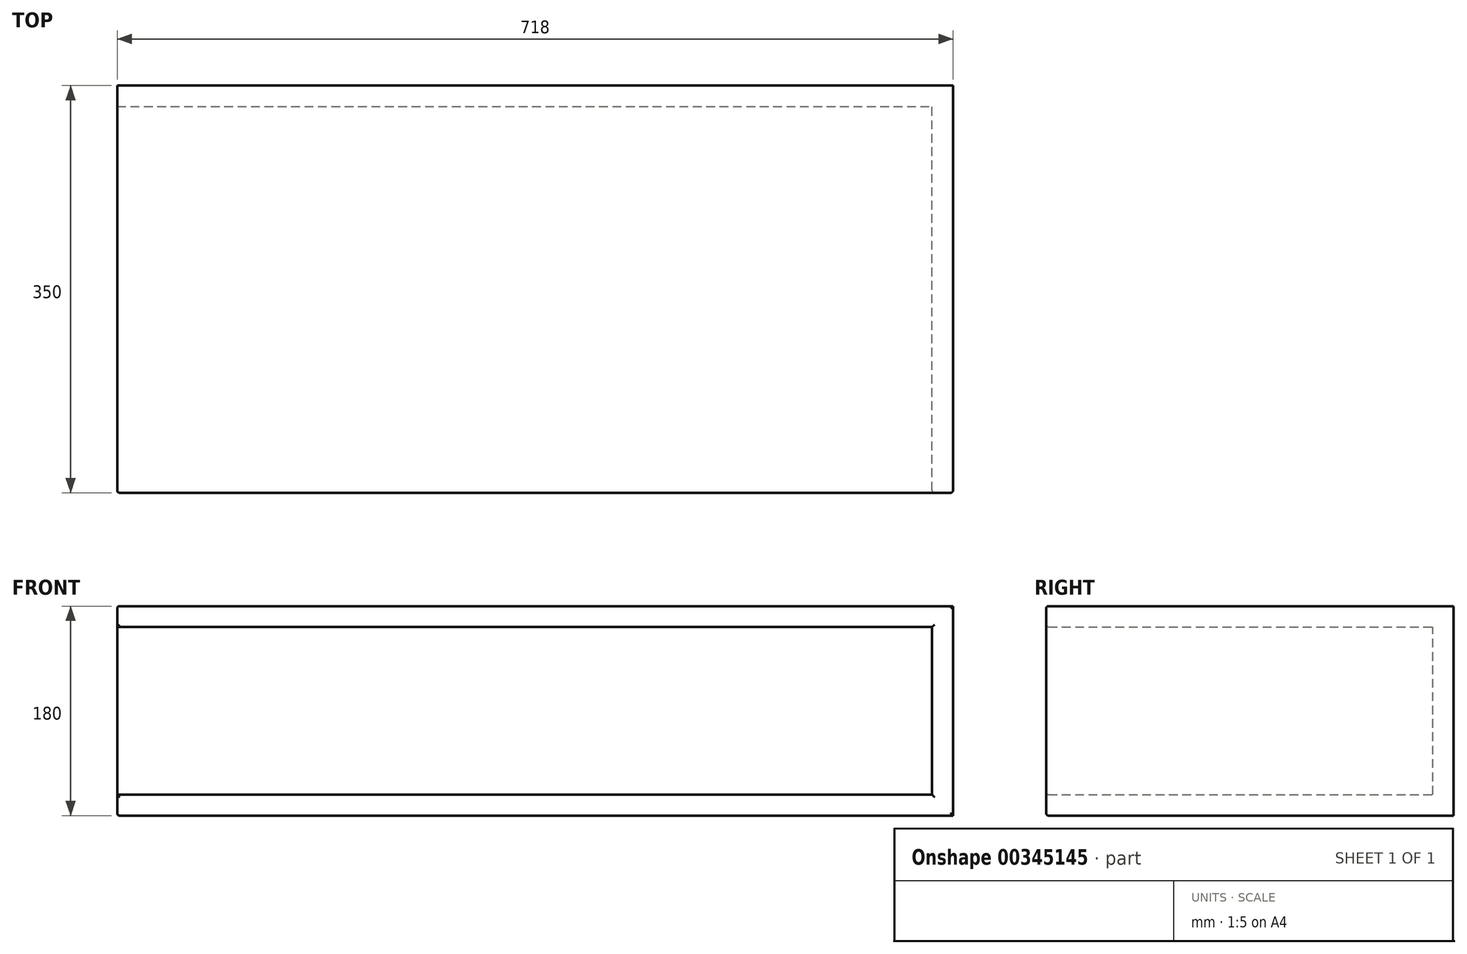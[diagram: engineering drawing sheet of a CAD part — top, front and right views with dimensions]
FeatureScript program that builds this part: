
annotation { "Feature Type Name" : "Feature", "Feature Type Description" : "" }
export const myFeature = defineFeature(function(context is Context, id is Id, definition is map)
    precondition{}
    {
        {
            var Q0;
            Q0=qCreatedBy(makeId("Front.planeOp"),FACE);
            var sketch = newSketch(context, id + "F0", { "sketchPlane" : qUnion([Q0])});
            skLineSegment(sketch, "E0.bottom", {"start": v(0, 0) * mm, "end": v(35.38, 0) * mm});
            skLineSegment(sketch, "E0.top", {"start": v(0, 39.43) * mm, "end": v(35.38, 39.43) * mm});
            skLineSegment(sketch, "E0.left", {"start": v(0, 0) * mm, "end": v(0, 39.43) * mm});
            skLineSegment(sketch, "E0.right", {"start": v(35.38, 0) * mm, "end": v(35.38, 39.43) * mm});
            skSolve(sketch);
        }
        {
            var Q0;
            Q0=makeQuery(id+"F0.imprint","IMPRINT",FACE,{"disambiguationData":[TD([[makeQuery(id+"F0.imprint","IMPRINT",EDGE,{"derivedFrom":sQuery(id+"F0.wireOp",EDGE,"E0.bottom")}),1.0]])]});
            extrude(context, id + "F1", {"entities" : qUnion([Q0]), "depth" : 350 * mm});
        }
        {
            var Q0;
            Q0=makeQuery(id+"F1.opExtrude","SWEPT_FACE",FACE,{"disambiguationData":[OSD([sQuery(id+"F0.wireOp",EDGE,"E0.left")])]});
            extrude(context, id + "F2", {"entities" : qUnion([Q0]), "operationType" : NewBodyOperationType.ADD, "oppositeDirection" : true, "depth" : 718 * mm});
        }
        {
            var Q0;
            {var subQ0=sQuery(id+"F0.wireOp",EDGE,"E0.bottom");Q0=makeQuery(id+"F2.boolean.opBoolean","MERGE",FACE,{"derivedFrom":[makeQuery(id+"F1.opExtrude","SWEPT_FACE",FACE,{"disambiguationData":[OSD([subQ0])]}),makeQuery(id+"F2.opExtrude","SWEPT_FACE",FACE,{"disambiguationData":[OSD([subQ0,sQuery(id+"F0.wireOp",EDGE,"E0.left")])]})]});}
            extrude(context, id + "F3", {"entities" : qUnion([Q0]), "operationType" : NewBodyOperationType.ADD, "oppositeDirection" : true, "depth" : 180 * mm});
        }
        {
            var Q0;
            {var subQ0=sQuery(id+"F0.wireOp",EDGE,"E0.left");var subQ1=sQuery(id+"F0.wireOp",EDGE,"E0.bottom");Q0=makeQuery(id+"F3.boolean.opBoolean","MERGE",FACE,{"derivedFrom":[makeQuery(id+"F2.boolean.opBoolean","MERGE",FACE,{"derivedFrom":[makeQuery(id+"F1.opExtrude","CAP_FACE",FACE,{"disambiguationData":[OSD([subQ1,sQuery(id+"F0.wireOp",EDGE,"E0.top"),subQ0,sQuery(id+"F0.wireOp",EDGE,"E0.right")])],"isStart":false}),makeQuery(id+"F2.opExtrude","SWEPT_FACE",FACE,{"disambiguationData":[OSD([subQ0]),TDD([makeQuery(id+"F1.opExtrude","CAP_EDGE",EDGE,{"disambiguationData":[OSD([subQ0])],"isStart":false})])]})]}),makeQuery(id+"F3.opExtrude","SWEPT_FACE",FACE,{"disambiguationData":[OSD([subQ1,subQ0]),TDD([makeQuery(id+"F2.boolean.opBoolean","MERGE",EDGE,{"derivedFrom":[makeQuery(id+"F1.opExtrude","CAP_EDGE",EDGE,{"disambiguationData":[OSD([subQ1])],"isStart":false}),makeQuery(id+"F2.opExtrude","SWEPT_EDGE",EDGE,{"disambiguationData":[OSD([subQ1,subQ0]),TDD([makeQuery(id+"F1.opExtrude","CAP_VERTEX",VERTEX,{"disambiguationData":[OSD([subQ1,subQ0])],"isStart":false})])]})]})])]})]});}
            var Q1;
            {var subQ0=sQuery(id+"F0.wireOp",EDGE,"E0.left");var subQ1=sQuery(id+"F0.wireOp",EDGE,"E0.bottom");Q1=makeQuery(id+"F3.boolean.opBoolean","MERGE",FACE,{"derivedFrom":[makeQuery(id+"F1.opExtrude","SWEPT_FACE",FACE,{"disambiguationData":[OSD([subQ0])]}),makeQuery(id+"F3.opExtrude","SWEPT_FACE",FACE,{"disambiguationData":[OSD([subQ1,subQ0]),TDD([makeQuery(id+"F1.opExtrude","SWEPT_EDGE",EDGE,{"disambiguationData":[OSD([subQ1,subQ0])]})])]})]});}
            shell(context, id + "F4", {"entities" : qUnion([Q0, Q1]), "thickness" : 18 * mm});
        }
        {
            var Q0;
            {var subQ0=sQuery(id+"F0.wireOp",EDGE,"E0.left");var subQ1=sQuery(id+"F0.wireOp",EDGE,"E0.bottom");Q0=makeQuery(id+"F3.opExtrude","CAP_EDGE",EDGE,{"disambiguationData":[OSD([subQ1,subQ0]),TDD([makeQuery(id+"F2.boolean.opBoolean","MERGE",EDGE,{"derivedFrom":[makeQuery(id+"F1.opExtrude","CAP_EDGE",EDGE,{"disambiguationData":[OSD([subQ1])],"isStart":false}),makeQuery(id+"F2.opExtrude","SWEPT_EDGE",EDGE,{"disambiguationData":[OSD([subQ1,subQ0]),TDD([makeQuery(id+"F1.opExtrude","CAP_VERTEX",VERTEX,{"disambiguationData":[OSD([subQ1,subQ0])],"isStart":false})])]})]})])],"isStart":false});}
            var Q1;
            {var subQ0=sQuery(id+"F0.wireOp",EDGE,"E0.left");var subQ1=sQuery(id+"F0.wireOp",EDGE,"E0.bottom");Q1=makeQuery(id+"F3.boolean.opBoolean","MERGE",EDGE,{"derivedFrom":[makeQuery(id+"F2.opExtrude","CAP_EDGE",EDGE,{"disambiguationData":[OSD([subQ0]),TDD([makeQuery(id+"F1.opExtrude","CAP_EDGE",EDGE,{"disambiguationData":[OSD([subQ0])],"isStart":false})])],"isStart":false}),makeQuery(id+"F3.opExtrude","SWEPT_EDGE",EDGE,{"disambiguationData":[OSD([subQ1,subQ0]),TDD([makeQuery(id+"F2.opExtrude","CAP_VERTEX",VERTEX,{"disambiguationData":[OSD([subQ1,subQ0]),TDD([makeQuery(id+"F1.opExtrude","CAP_VERTEX",VERTEX,{"disambiguationData":[OSD([subQ1,subQ0])],"isStart":false})])],"isStart":false})])]})]});}
            var Q2;
            {var subQ0=sQuery(id+"F0.wireOp",EDGE,"E0.left");var subQ1=sQuery(id+"F0.wireOp",EDGE,"E0.bottom");Q2=makeQuery(id+"F2.boolean.opBoolean","MERGE",EDGE,{"derivedFrom":[makeQuery(id+"F1.opExtrude","CAP_EDGE",EDGE,{"disambiguationData":[OSD([subQ1])],"isStart":false}),makeQuery(id+"F2.opExtrude","SWEPT_EDGE",EDGE,{"disambiguationData":[OSD([subQ1,subQ0]),TDD([makeQuery(id+"F1.opExtrude","CAP_VERTEX",VERTEX,{"disambiguationData":[OSD([subQ1,subQ0])],"isStart":false})])]})]});}
            fillet(context, id + "F5", {"entities" : qUnion([Q0, Q1, Q2]), "radius" : 2 * mm, "tangentPropagation" : true, "allowEdgeOverflow" : false});
        }
        {
            var Q0;
            {var subQ0=sQuery(id+"F0.wireOp",EDGE,"E0.left");var subQ1=sQuery(id+"F0.wireOp",EDGE,"E0.bottom");Q0=makeQuery(id+"F4.opShell","OFFSET_EDGE",EDGE,{"disambiguationData":[OSD([subQ1,subQ0]),TDD([makeQuery(id+"F3.boolean.opBoolean","MERGE",EDGE,{"derivedFrom":[makeQuery(id+"F2.opExtrude","CAP_EDGE",EDGE,{"disambiguationData":[OSD([subQ0]),TDD([makeQuery(id+"F1.opExtrude","CAP_EDGE",EDGE,{"disambiguationData":[OSD([subQ0])],"isStart":false})])],"isStart":false}),makeQuery(id+"F3.opExtrude","SWEPT_EDGE",EDGE,{"disambiguationData":[OSD([subQ1,subQ0]),TDD([makeQuery(id+"F2.opExtrude","CAP_VERTEX",VERTEX,{"disambiguationData":[OSD([subQ1,subQ0]),TDD([makeQuery(id+"F1.opExtrude","CAP_VERTEX",VERTEX,{"disambiguationData":[OSD([subQ1,subQ0])],"isStart":false})])],"isStart":false})])]})]})])]});}
            var Q1;
            {var subQ0=sQuery(id+"F0.wireOp",EDGE,"E0.left");var subQ1=sQuery(id+"F0.wireOp",EDGE,"E0.bottom");Q1=makeQuery(id+"F4.opShell","OFFSET_EDGE",EDGE,{"disambiguationData":[OSD([subQ1,subQ0]),TDD([makeQuery(id+"F3.opExtrude","CAP_EDGE",EDGE,{"disambiguationData":[OSD([subQ1,subQ0]),TDD([makeQuery(id+"F2.boolean.opBoolean","MERGE",EDGE,{"derivedFrom":[makeQuery(id+"F1.opExtrude","CAP_EDGE",EDGE,{"disambiguationData":[OSD([subQ1])],"isStart":false}),makeQuery(id+"F2.opExtrude","SWEPT_EDGE",EDGE,{"disambiguationData":[OSD([subQ1,subQ0]),TDD([makeQuery(id+"F1.opExtrude","CAP_VERTEX",VERTEX,{"disambiguationData":[OSD([subQ1,subQ0])],"isStart":false})])]})]})])],"isStart":false})])]});}
            var Q2;
            {var subQ0=sQuery(id+"F0.wireOp",EDGE,"E0.left");var subQ1=sQuery(id+"F0.wireOp",EDGE,"E0.bottom");Q2=makeQuery(id+"F4.opShell","OFFSET_EDGE",EDGE,{"disambiguationData":[OSD([subQ1,subQ0]),TDD([makeQuery(id+"F2.boolean.opBoolean","MERGE",EDGE,{"derivedFrom":[makeQuery(id+"F1.opExtrude","CAP_EDGE",EDGE,{"disambiguationData":[OSD([subQ1])],"isStart":false}),makeQuery(id+"F2.opExtrude","SWEPT_EDGE",EDGE,{"disambiguationData":[OSD([subQ1,subQ0]),TDD([makeQuery(id+"F1.opExtrude","CAP_VERTEX",VERTEX,{"disambiguationData":[OSD([subQ1,subQ0])],"isStart":false})])]})]})])]});}
            var Q3;
            {var subQ0=sQuery(id+"F0.wireOp",EDGE,"E0.left");var subQ1=sQuery(id+"F0.wireOp",EDGE,"E0.bottom");Q3=makeQuery(id+"F4.opShell","OFFSET_EDGE",EDGE,{"disambiguationData":[OSD([subQ1,subQ0]),TDD([makeQuery(id+"F3.boolean.opBoolean","MERGE",EDGE,{"derivedFrom":[makeQuery(id+"F1.opExtrude","CAP_EDGE",EDGE,{"disambiguationData":[OSD([subQ0])],"isStart":false}),makeQuery(id+"F3.opExtrude","SWEPT_EDGE",EDGE,{"disambiguationData":[OSD([subQ1,subQ0]),TDD([makeQuery(id+"F1.opExtrude","CAP_VERTEX",VERTEX,{"disambiguationData":[OSD([subQ1,subQ0])],"isStart":false})])]})]})])]});}
            var Q4;
            {var subQ0=sQuery(id+"F0.wireOp",EDGE,"E0.left");var subQ1=sQuery(id+"F0.wireOp",EDGE,"E0.bottom");Q4=makeQuery(id+"F3.boolean.opBoolean","MERGE",EDGE,{"derivedFrom":[makeQuery(id+"F1.opExtrude","CAP_EDGE",EDGE,{"disambiguationData":[OSD([subQ0])],"isStart":false}),makeQuery(id+"F3.opExtrude","SWEPT_EDGE",EDGE,{"disambiguationData":[OSD([subQ1,subQ0]),TDD([makeQuery(id+"F1.opExtrude","CAP_VERTEX",VERTEX,{"disambiguationData":[OSD([subQ1,subQ0])],"isStart":false})])]})]});}
            fillet(context, id + "F6", {"entities" : qUnion([Q0, Q1, Q2, Q3, Q4]), "radius" : 2 * mm, "tangentPropagation" : true, "allowEdgeOverflow" : false});
        }
    });
